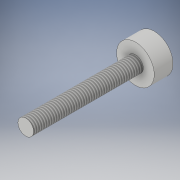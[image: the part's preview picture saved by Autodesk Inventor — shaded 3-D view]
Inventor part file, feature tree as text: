
AUTODESK INVENTOR PART (.ipt)
format: ipt  version: 2018 (Build 220112000, 112)  size: 107,008 bytes
history: native  units: in
note: dims shown in document units (in); Inventor stores cm internally (conversion verified against a paired STEP export)
features: revolve x1, thread x1, sketch x1
ambient origin geometry x8: Origin, YZ Plane, XZ Plane, XY Plane, X Axis, Y Axis, Z Axis, Center Point
bodies: Solid1 (feature_tree)
feature tree (3):
  revolve  "Revolution1"  [1 undecoded]
  thread  "Thread1"  [1 undecoded]
  sketch  "Sketch1"  dims[d0=0.0984in d1=1.378in d2=0.2362in d3=0.2362in d4=90.0deg d5=0.3937in d6=0.0in]
note: 2 required parameter values undecoded (feature->parameter linkage not recoverable at this tier; creation-order binding heuristic only, values carry confidence <= 0.55)